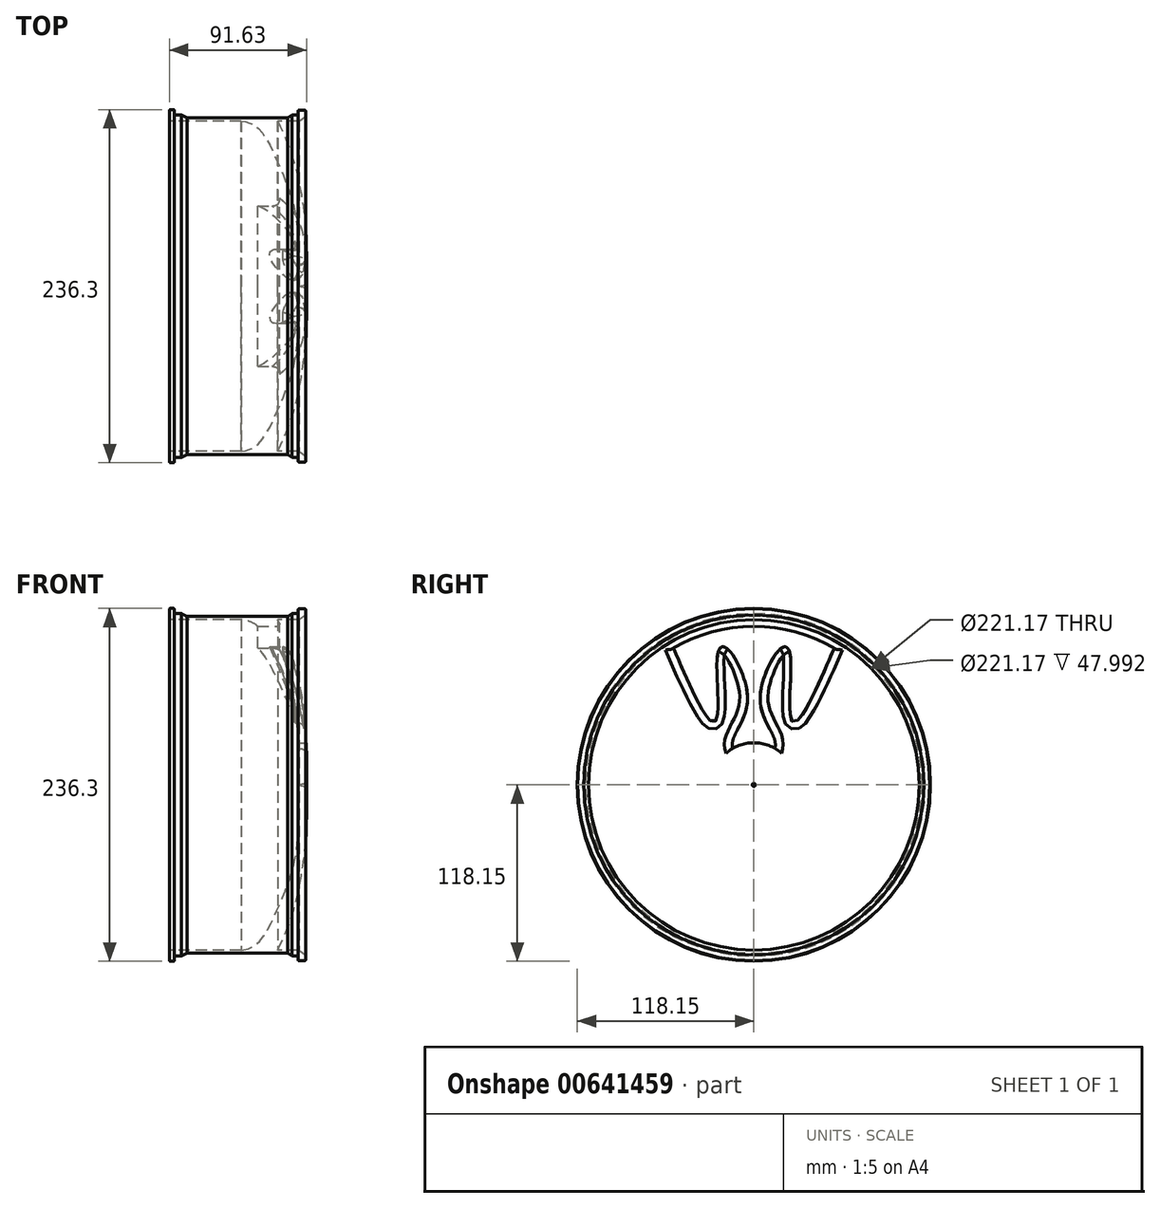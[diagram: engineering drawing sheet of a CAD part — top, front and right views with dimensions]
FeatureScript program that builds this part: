
annotation { "Feature Type Name" : "Feature", "Feature Type Description" : "" }
export const myFeature = defineFeature(function(context is Context, id is Id, definition is map)
    precondition{}
    {
        {
            var Q0;
            Q0=qCreatedBy(makeId("Front.planeOp"),FACE);
            var sketch = newSketch(context, id + "F0", { "sketchPlane" : qUnion([Q0])});
            skFitSpline(sketch, "E0", {"points": [v(-4.6, 0) * mm, v(-4.73, 27.03) * mm, v(-7.65, 52.48) * mm, v(-17.43, 80.2) * mm, v(-32.37, 106.41) * mm, v(-43.06, 110.59) * mm], "startDerivative": vector(-1.03, 134.1) * mm, "endDerivative": vector(-78.68, 13.68) * mm});
            skLineSegment(sketch, "E1", {"start": v(-43.06, 110.59) * mm, "end": v(-91.05, 110.59) * mm});
            skLineSegment(sketch, "E2", {"start": v(-91.05, 110.59) * mm, "end": v(-91.05, 118.15) * mm});
            skLineSegment(sketch, "E3", {"start": v(-91.05, 118.15) * mm, "end": v(-87.83, 118.15) * mm});
            skLineSegment(sketch, "E4", {"start": v(-87.83, 118.15) * mm, "end": v(-87.83, 114.64) * mm});
            skLineSegment(sketch, "E5", {"start": v(-87.83, 114.64) * mm, "end": v(-83, 114.64) * mm});
            skLineSegment(sketch, "E6", {"start": v(-83, 114.64) * mm, "end": v(-79.27, 112.67) * mm});
            skLineSegment(sketch, "E7", {"start": v(-79.27, 112.67) * mm, "end": v(-11.93, 112.67) * mm});
            skLineSegment(sketch, "E8", {"start": v(-11.93, 112.67) * mm, "end": v(-8.95, 114.64) * mm});
            skLineSegment(sketch, "E9", {"start": v(-8.95, 114.64) * mm, "end": v(-4.98, 114.64) * mm});
            skLineSegment(sketch, "E10", {"start": v(-4.98, 114.64) * mm, "end": v(-4.98, 117.78) * mm});
            skLineSegment(sketch, "E11", {"start": v(-4.98, 117.78) * mm, "end": v(0, 117.78) * mm});
            skFitSpline(sketch, "E12", {"points": [v(0, 1.06) * mm, v(0, 38.3) * mm, v(-8.05, 83.9) * mm, v(-18.6, 110.59) * mm], "startDerivative": vector(4.5, 106.43) * mm, "endDerivative": vector(-38.04, 82.82) * mm});
            skLineSegment(sketch, "E13", {"start": v(-18.6, 110.59) * mm, "end": v(-4.24, 110.59) * mm});
            skLineSegment(sketch, "E14", {"start": v(-4.24, 110.59) * mm, "end": v(0, 113.78) * mm});
            skLineSegment(sketch, "E15", {"start": v(0, 113.78) * mm, "end": v(0, 117.78) * mm});
            skLineSegment(sketch, "E16", {"start": v(-4.6, 0.09) * mm, "end": v(0, 1.06) * mm});
            skLineSegment(sketch, "E17", {"start": v(-4.6, 0) * mm, "end": v(0, 0) * mm});
            skSolve(sketch);
        }
        {
            var Q0;
            {var subQ0=sQuery(id+"F0.wireOp",EDGE,"E0");Q0=makeQuery(id+"F0.imprint","IMPRINT",FACE,{"disambiguationData":[TD([[makeQuery(id+"F0.imprint","IMPRINT",EDGE,{"derivedFrom":subQ0}),-1.0]])]});}
            var Q1;
            Q1=sQuery(id+"F0.wireOp",EDGE,"E17");
            revolve(context, id + "F1", {"entities" : qUnion([Q0]), "axis" : qUnion([Q1]), "revolveType" : RevolveType.FULL});
        }
        {
            var Q0;
            Q0=makeQuery(id+"F1.opRevolve","SWEPT_EDGE",EDGE,{"disambiguationData":[OSD([sQuery(id+"F0.wireOp",EDGE,"E2"),sQuery(id+"F0.wireOp",EDGE,"E3")])]});
            var Q1;
            Q1=makeQuery(id+"F1.opRevolve","SWEPT_EDGE",EDGE,{"disambiguationData":[OSD([sQuery(id+"F0.wireOp",EDGE,"E3"),sQuery(id+"F0.wireOp",EDGE,"E4")])]});
            var Q2;
            Q2=makeQuery(id+"F1.opRevolve","SWEPT_EDGE",EDGE,{"disambiguationData":[OSD([sQuery(id+"F0.wireOp",EDGE,"E10"),sQuery(id+"F0.wireOp",EDGE,"E11")])]});
            var Q3;
            Q3=makeQuery(id+"F1.opRevolve","SWEPT_EDGE",EDGE,{"disambiguationData":[OSD([sQuery(id+"F0.wireOp",EDGE,"E11"),sQuery(id+"F0.wireOp",EDGE,"NlqiYfBz-LXvw-5fZl-1wZW-JZulMop75H53")])]});
            fillet(context, id + "F2", {"entities" : qUnion([Q0, Q1, Q2, Q3]), "radius" : 0.5 * mm, "tangentPropagation" : true, "allowEdgeOverflow" : false});
        }
        {
            var Q0;
            Q0=qCreatedBy(makeId("Right.planeOp"),FACE);
            var sketch = newSketch(context, id + "F3", { "sketchPlane" : qUnion([Q0])});
            skCircle(sketch, "E18", {"center": v(0, 0) * mm, "radius": 106.16 * mm});
            skFitSpline(sketch, "E19", {"points": [v(-53.72, 91.56) * mm, v(-24.59, 84.61) * mm, v(-4.6, 62.83) * mm, v(-14.12, 24.36) * mm], "startDerivative": vector(377.61, -901.75) * mm, "endDerivative": vector(21.09, -84.33) * mm});
            skCircle(sketch, "E20", {"center": v(0, 0) * mm, "radius": 28.16 * mm});
            skLineSegment(sketch, "E21", {"start": v(0, 28.16) * mm, "end": v(0, 106.16) * mm, "construction": true});
            skFitSpline(sketch, "E22.MirrorCS", {"points": [v(53.72, 91.56) * mm, v(24.59, 84.61) * mm, v(4.6, 62.83) * mm, v(14.12, 24.36) * mm], "startDerivative": vector(-377.61, -901.75) * mm, "endDerivative": vector(-21.09, -84.33) * mm});
            skLineSegment(sketch, "E23.1.0", {"start": v(-24.39, -14.08) * mm, "end": v(-91.94, -53.08) * mm, "construction": true});
            skLineSegment(sketch, "E23.2.0", {"start": v(24.39, -14.08) * mm, "end": v(91.94, -53.08) * mm, "construction": true});
            skSolve(sketch);
        }
        {
            var Q0;
            {var subQ0=sQuery(id+"F3.wireOp",EDGE,"E19");Q0=makeQuery(id+"F3.imprint","IMPRINT",FACE,{"disambiguationData":[TD([[makeQuery(id+"F3.imprint","IMPRINT",EDGE,{"derivedFrom":subQ0}),1.0]])]});}
            var Q1;
            Q1=makeQuery(id+"F1.opRevolve","SWEPT_FACE",FACE,{"disambiguationData":[OSD([sQuery(id+"F0.wireOp",EDGE,"E0")])]});
            extrude(context, id + "F4", {"entities" : qUnion([Q0]), "operationType" : NewBodyOperationType.REMOVE, "endBound" : BoundingType.SYMMETRIC, "oppositeDirection" : true, "depth" : 76.2 * mm, "endBoundEntityFace" : qUnion([Q1]), "offsetDistance" : 25.4 * mm});
        }
        {
            var Q0;
            Q0=makeQuery(id+"F4.boolean.opBoolean","INTERSECT",EDGE,{"derivedFrom":[makeQuery(id+"F1.opRevolve","SWEPT_FACE",FACE,{"disambiguationData":[OSD([sQuery(id+"F0.wireOp",EDGE,"E12")])]}),makeQuery(id+"F4.opExtrude","SWEPT_FACE",FACE,{"disambiguationData":[OSD([sQuery(id+"F3.wireOp",EDGE,"E22.MirrorCS")])]})]});
            var Q1;
            Q1=makeQuery(id+"F4.boolean.opBoolean","INTERSECT",EDGE,{"derivedFrom":[makeQuery(id+"F1.opRevolve","SWEPT_FACE",FACE,{"disambiguationData":[OSD([sQuery(id+"F0.wireOp",EDGE,"E12")])]}),makeQuery(id+"F4.opExtrude","SWEPT_FACE",FACE,{"disambiguationData":[OSD([sQuery(id+"F3.wireOp",EDGE,"E19")])]})]});
            fillet(context, id + "F5", {"entities" : qUnion([Q0, Q1]), "radius" : 5.08 * mm, "tangentPropagation" : true, "allowEdgeOverflow" : false});
        }
        {
            var Q0;
            Q0=makeQuery(id+"F4.boolean.opBoolean","INTERSECT",EDGE,{"derivedFrom":[makeQuery(id+"F1.opRevolve","SWEPT_FACE",FACE,{"disambiguationData":[OSD([sQuery(id+"F0.wireOp",EDGE,"E12")])]}),makeQuery(id+"F4.opExtrude","SWEPT_FACE",FACE,{"disambiguationData":[OSD([sQuery(id+"F3.wireOp",EDGE,"E18")])]})]});
            fillet(context, id + "F6", {"entities" : qUnion([Q0]), "radius" : 1.27 * mm, "tangentPropagation" : true, "allowEdgeOverflow" : false});
        }
    });
